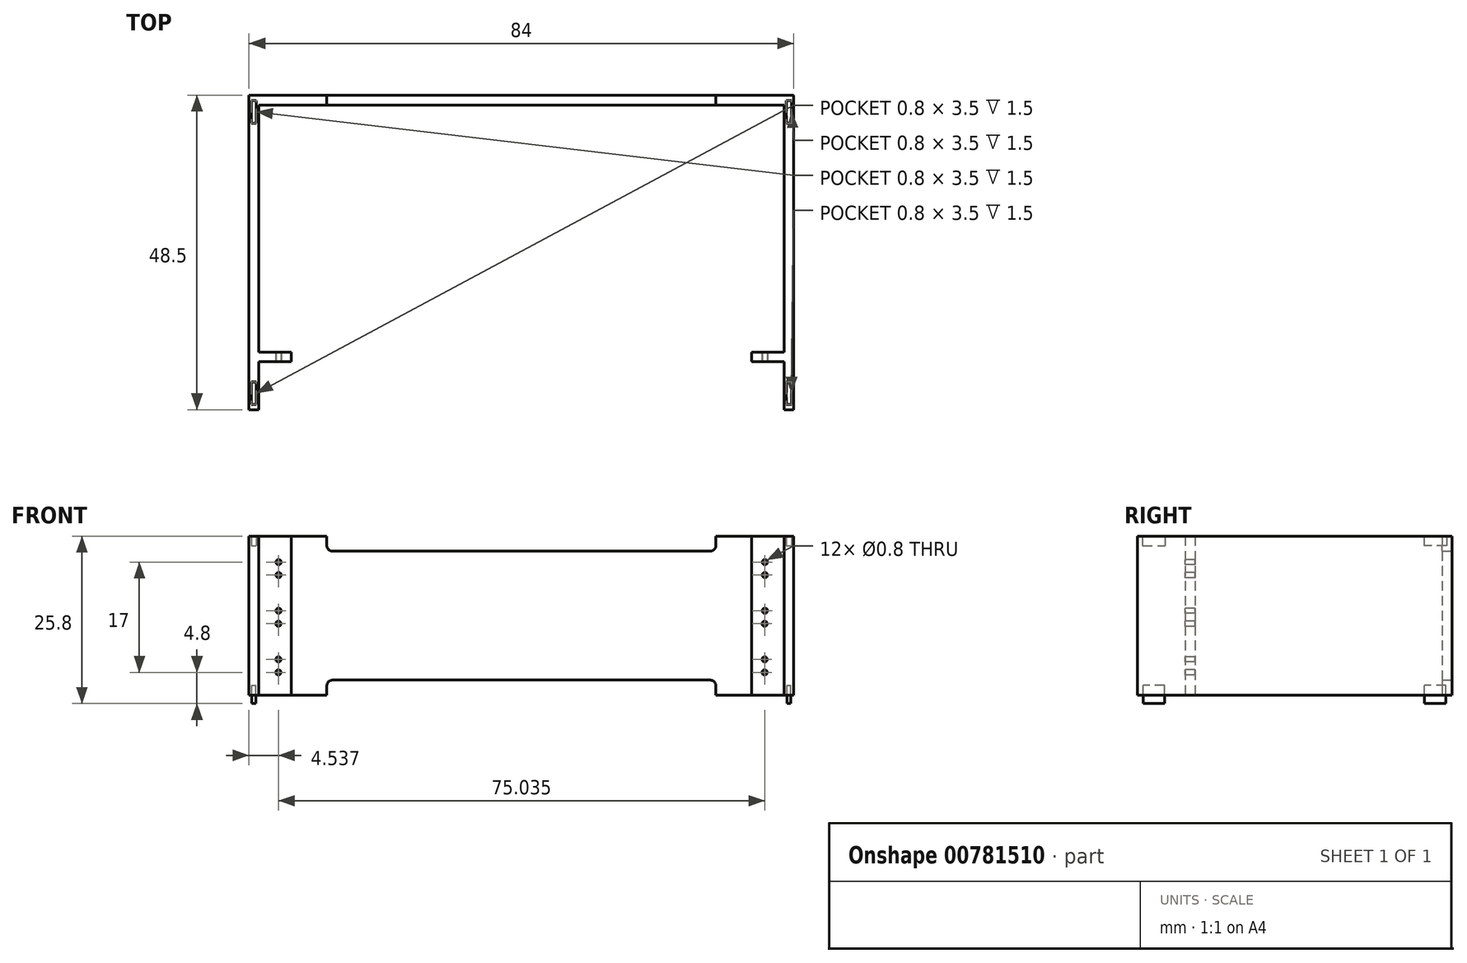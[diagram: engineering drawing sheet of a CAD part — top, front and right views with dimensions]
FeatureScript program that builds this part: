
annotation { "Feature Type Name" : "Feature", "Feature Type Description" : "" }
export const myFeature = defineFeature(function(context is Context, id is Id, definition is map)
    precondition{}
    {
        {
            var Q0;
            Q0=qCreatedBy(makeId("Top.planeOp"),FACE);
            var sketch = newSketch(context, id + "F0", { "sketchPlane" : qUnion([Q0])});
            skLineSegment(sketch, "E0.bottom", {"start": v(-40.55, -23.12) * mm, "end": v(-42.05, -23.12) * mm});
            skLineSegment(sketch, "E0.top", {"start": v(-40.55, 23.88) * mm, "end": v(-42.05, 23.88) * mm});
            skLineSegment(sketch, "E0.left", {"start": v(-40.55, -23.12) * mm, "end": v(-40.55, 23.88) * mm});
            skLineSegment(sketch, "E0.right", {"start": v(-42.05, -23.12) * mm, "end": v(-42.05, 23.88) * mm});
            skLineSegment(sketch, "E1.bottom", {"start": v(40.45, -23.12) * mm, "end": v(41.95, -23.12) * mm});
            skLineSegment(sketch, "E1.top", {"start": v(40.45, 23.88) * mm, "end": v(41.95, 23.88) * mm});
            skLineSegment(sketch, "E1.left", {"start": v(40.45, -23.12) * mm, "end": v(40.45, 23.88) * mm});
            skLineSegment(sketch, "E1.right", {"start": v(41.95, -23.12) * mm, "end": v(41.95, 23.88) * mm});
            skLineSegment(sketch, "E2.bottom", {"start": v(41.95, 23.88) * mm, "end": v(-42.05, 23.88) * mm});
            skLineSegment(sketch, "E2.top", {"start": v(41.95, 25.38) * mm, "end": v(-42.05, 25.38) * mm});
            skLineSegment(sketch, "E2.left", {"start": v(41.95, 23.88) * mm, "end": v(41.95, 25.38) * mm});
            skLineSegment(sketch, "E2.right", {"start": v(-42.05, 23.88) * mm, "end": v(-42.05, 25.38) * mm});
            skLineSegment(sketch, "E3.bottom", {"start": v(-40.55, -14.22) * mm, "end": v(-35.55, -14.22) * mm});
            skLineSegment(sketch, "E3.top", {"start": v(-40.55, -15.72) * mm, "end": v(-35.55, -15.72) * mm});
            skLineSegment(sketch, "E3.left", {"start": v(-40.55, -14.22) * mm, "end": v(-40.55, -15.72) * mm});
            skLineSegment(sketch, "E3.right", {"start": v(-35.55, -14.22) * mm, "end": v(-35.55, -15.72) * mm});
            skLineSegment(sketch, "E4.bottom", {"start": v(35.45, -15.72) * mm, "end": v(40.45, -15.72) * mm});
            skLineSegment(sketch, "E4.top", {"start": v(35.45, -14.22) * mm, "end": v(40.45, -14.22) * mm});
            skLineSegment(sketch, "E4.left", {"start": v(35.45, -15.72) * mm, "end": v(35.45, -14.22) * mm});
            skLineSegment(sketch, "E4.right", {"start": v(40.45, -15.72) * mm, "end": v(40.45, -14.22) * mm});
            skLineSegment(sketch, "E5.bottom", {"start": v(-41.7, -22.32) * mm, "end": v(-40.9, -22.32) * mm});
            skLineSegment(sketch, "E5.top", {"start": v(-41.7, -18.82) * mm, "end": v(-40.9, -18.82) * mm});
            skLineSegment(sketch, "E5.left", {"start": v(-41.7, -22.32) * mm, "end": v(-41.7, -18.82) * mm});
            skLineSegment(sketch, "E5.right", {"start": v(-40.9, -22.32) * mm, "end": v(-40.9, -18.82) * mm});
            skLineSegment(sketch, "E6.bottom", {"start": v(-41.7, 24.58) * mm, "end": v(-40.9, 24.58) * mm});
            skLineSegment(sketch, "E6.top", {"start": v(-41.7, 21.08) * mm, "end": v(-40.9, 21.08) * mm});
            skLineSegment(sketch, "E6.left", {"start": v(-41.7, 24.58) * mm, "end": v(-41.7, 21.08) * mm});
            skLineSegment(sketch, "E6.right", {"start": v(-40.9, 24.58) * mm, "end": v(-40.9, 21.08) * mm});
            skLineSegment(sketch, "E7.bottom", {"start": v(40.8, 24.58) * mm, "end": v(41.6, 24.58) * mm});
            skLineSegment(sketch, "E7.top", {"start": v(40.8, 21.08) * mm, "end": v(41.6, 21.08) * mm});
            skLineSegment(sketch, "E7.left", {"start": v(40.8, 24.58) * mm, "end": v(40.8, 21.08) * mm});
            skLineSegment(sketch, "E7.right", {"start": v(41.6, 24.58) * mm, "end": v(41.6, 21.08) * mm});
            skLineSegment(sketch, "E8.bottom", {"start": v(40.8, -18.82) * mm, "end": v(41.6, -18.82) * mm});
            skLineSegment(sketch, "E8.top", {"start": v(40.8, -22.32) * mm, "end": v(41.6, -22.32) * mm});
            skLineSegment(sketch, "E8.left", {"start": v(40.8, -18.82) * mm, "end": v(40.8, -22.32) * mm});
            skLineSegment(sketch, "E8.right", {"start": v(41.6, -18.82) * mm, "end": v(41.6, -22.32) * mm});
            skLineSegment(sketch, "E9.bottom", {"start": v(-41.6, -18.92) * mm, "end": v(-41, -18.92) * mm});
            skLineSegment(sketch, "E9.top", {"start": v(-41.6, -22.22) * mm, "end": v(-41, -22.22) * mm});
            skLineSegment(sketch, "E9.left", {"start": v(-41.6, -18.92) * mm, "end": v(-41.6, -22.22) * mm});
            skLineSegment(sketch, "E9.right", {"start": v(-41, -18.92) * mm, "end": v(-41, -22.22) * mm});
            skLineSegment(sketch, "E10.bottom", {"start": v(-41.6, 24.48) * mm, "end": v(-41, 24.48) * mm});
            skLineSegment(sketch, "E10.top", {"start": v(-41.6, 21.18) * mm, "end": v(-41, 21.18) * mm});
            skLineSegment(sketch, "E10.left", {"start": v(-41.6, 24.48) * mm, "end": v(-41.6, 21.18) * mm});
            skLineSegment(sketch, "E10.right", {"start": v(-41, 24.48) * mm, "end": v(-41, 21.18) * mm});
            skLineSegment(sketch, "E11.bottom", {"start": v(40.9, 24.48) * mm, "end": v(41.5, 24.48) * mm});
            skLineSegment(sketch, "E11.top", {"start": v(40.9, 21.18) * mm, "end": v(41.5, 21.18) * mm});
            skLineSegment(sketch, "E11.left", {"start": v(40.9, 24.48) * mm, "end": v(40.9, 21.18) * mm});
            skLineSegment(sketch, "E11.right", {"start": v(41.5, 24.48) * mm, "end": v(41.5, 21.18) * mm});
            skLineSegment(sketch, "E12.bottom", {"start": v(40.9, -18.92) * mm, "end": v(41.5, -18.92) * mm});
            skLineSegment(sketch, "E12.top", {"start": v(40.9, -22.22) * mm, "end": v(41.5, -22.22) * mm});
            skLineSegment(sketch, "E12.left", {"start": v(40.9, -18.92) * mm, "end": v(40.9, -22.22) * mm});
            skLineSegment(sketch, "E12.right", {"start": v(41.5, -18.92) * mm, "end": v(41.5, -22.22) * mm});
            skSolve(sketch);
        }
        {
            var Q0;
            Q0=makeQuery(id+"F0.imprint","IMPRINT",FACE,{"disambiguationData":[TD([[makeQuery(id+"F0.imprint","IMPRINT",EDGE,{"derivedFrom":sQuery(id+"F0.wireOp",EDGE,"E3.bottom")}),-1.0]])]});
            var Q1;
            {var subQ5=sQuery(id+"F0.wireOp",EDGE,"E0.bottom");Q1=makeQuery(id+"F0.imprint","IMPRINT",FACE,{"disambiguationData":[TD([[makeQuery(id+"F0.imprint","IMPRINT",EDGE,{"derivedFrom":subQ5}),-1.0]])]});}
            var Q2;
            Q2=makeQuery(id+"F0.imprint","IMPRINT",FACE,{"disambiguationData":[TD([[makeQuery(id+"F0.imprint","IMPRINT",EDGE,{"derivedFrom":sQuery(id+"F0.wireOp",EDGE,"E2.top")}),1.0]])]});
            var Q3;
            {var subQ5=sQuery(id+"F0.wireOp",EDGE,"E1.bottom");Q3=makeQuery(id+"F0.imprint","IMPRINT",FACE,{"disambiguationData":[TD([[makeQuery(id+"F0.imprint","IMPRINT",EDGE,{"derivedFrom":subQ5}),1.0]])]});}
            var Q4;
            Q4=makeQuery(id+"F0.imprint","IMPRINT",FACE,{"disambiguationData":[TD([[makeQuery(id+"F0.imprint","IMPRINT",EDGE,{"derivedFrom":sQuery(id+"F0.wireOp",EDGE,"E4.bottom")}),1.0]])]});
            var Q5;
            Q5=makeQuery(id+"F0.imprint","IMPRINT",FACE,{"disambiguationData":[TD([[makeQuery(id+"F0.imprint","IMPRINT",EDGE,{"derivedFrom":sQuery(id+"F0.wireOp",EDGE,"E5.bottom")}),1.0]])]});
            var Q6;
            Q6=makeQuery(id+"F0.imprint","IMPRINT",FACE,{"disambiguationData":[TD([[makeQuery(id+"F0.imprint","IMPRINT",EDGE,{"derivedFrom":sQuery(id+"F0.wireOp",EDGE,"E8.bottom")}),-1.0]])]});
            var Q7;
            {var subQ5=sQuery(id+"F0.wireOp",EDGE,"E7.top");Q7=makeQuery(id+"F0.imprint","IMPRINT",FACE,{"disambiguationData":[TD([[makeQuery(id+"F0.imprint","IMPRINT",EDGE,{"derivedFrom":subQ5}),1.0]])]});}
            var Q8;
            {var subQ5=sQuery(id+"F0.wireOp",EDGE,"E7.bottom");Q8=makeQuery(id+"F0.imprint","IMPRINT",FACE,{"disambiguationData":[TD([[makeQuery(id+"F0.imprint","IMPRINT",EDGE,{"derivedFrom":subQ5}),-1.0]])]});}
            var Q9;
            {var subQ5=sQuery(id+"F0.wireOp",EDGE,"E6.bottom");Q9=makeQuery(id+"F0.imprint","IMPRINT",FACE,{"disambiguationData":[TD([[makeQuery(id+"F0.imprint","IMPRINT",EDGE,{"derivedFrom":subQ5}),-1.0]])]});}
            var Q10;
            {var subQ5=sQuery(id+"F0.wireOp",EDGE,"E6.top");Q10=makeQuery(id+"F0.imprint","IMPRINT",FACE,{"disambiguationData":[TD([[makeQuery(id+"F0.imprint","IMPRINT",EDGE,{"derivedFrom":subQ5}),1.0]])]});}
            var Q11;
            Q11=makeQuery(id+"F0.imprint","IMPRINT",FACE,{"disambiguationData":[TD([[makeQuery(id+"F0.imprint","IMPRINT",EDGE,{"derivedFrom":sQuery(id+"F0.wireOp",EDGE,"E9.bottom")}),-1.0]])]});
            var Q12;
            {var subQ5=sQuery(id+"F0.wireOp",EDGE,"E10.top");Q12=makeQuery(id+"F0.imprint","IMPRINT",FACE,{"disambiguationData":[TD([[makeQuery(id+"F0.imprint","IMPRINT",EDGE,{"derivedFrom":subQ5}),1.0]])]});}
            var Q13;
            Q13=makeQuery(id+"F0.imprint","IMPRINT",FACE,{"disambiguationData":[TD([[makeQuery(id+"F0.imprint","IMPRINT",EDGE,{"derivedFrom":sQuery(id+"F0.wireOp",EDGE,"E12.bottom")}),-1.0]])]});
            var Q14;
            {var subQ5=sQuery(id+"F0.wireOp",EDGE,"E11.top");Q14=makeQuery(id+"F0.imprint","IMPRINT",FACE,{"disambiguationData":[TD([[makeQuery(id+"F0.imprint","IMPRINT",EDGE,{"derivedFrom":subQ5}),1.0]])]});}
            var Q15;
            {var subQ5=sQuery(id+"F0.wireOp",EDGE,"E11.bottom");Q15=makeQuery(id+"F0.imprint","IMPRINT",FACE,{"disambiguationData":[TD([[makeQuery(id+"F0.imprint","IMPRINT",EDGE,{"derivedFrom":subQ5}),-1.0]])]});}
            var Q16;
            {var subQ5=sQuery(id+"F0.wireOp",EDGE,"E10.bottom");Q16=makeQuery(id+"F0.imprint","IMPRINT",FACE,{"disambiguationData":[TD([[makeQuery(id+"F0.imprint","IMPRINT",EDGE,{"derivedFrom":subQ5}),-1.0]])]});}
            extrude(context, id + "F1", {"entities" : qUnion([Q0, Q1, Q2, Q3, Q4, Q5, Q6, Q7, Q8, Q9, Q10, Q11, Q12, Q13, Q14, Q15, Q16]), "depth" : 23 * mm, "offsetDistance" : 25 * mm, "hasSecondDirection" : true, "secondDirectionOppositeDirection" : true, "secondDirectionDepth" : 1.5 * mm});
        }
        {
            var Q0;
            Q0=makeQuery(id+"F1.opExtrude","SWEPT_FACE",FACE,{"disambiguationData":[OSD([sQuery(id+"F0.wireOp",EDGE,"E3.top")])]});
            var sketch = newSketch(context, id + "F2", { "sketchPlane" : qUnion([Q0])});
            skPoint(sketch, "E13", {"position": v(-37.51, 4) * mm});
            skPoint(sketch, "E14", {"position": v(-37.51, 2) * mm});
            skPoint(sketch, "E15", {"position": v(-37.48, 11.5) * mm});
            skPoint(sketch, "E16", {"position": v(-37.51, 9.5) * mm});
            skPoint(sketch, "E17", {"position": v(-37.48, 19) * mm});
            skPoint(sketch, "E18", {"position": v(-37.48, 17) * mm});
            skSolve(sketch);
        }
        {
            var Q0;
            Q0=sQuery(id+"F2.wireOp",VERTEX,"88589781-5102-4832-97d8-1e510481dceb");
            var Q1;
            Q1=sQuery(id+"F2.wireOp",VERTEX,"56790afe-c75e-4d87-a7f2-a835bb2694d8");
            var Q2;
            Q2=sQuery(id+"F2.wireOp",VERTEX,"4a0b0304-49c9-424d-a3fc-b7b72423f08e");
            var Q3;
            Q3=sQuery(id+"F2.wireOp",VERTEX,"8470db93-98b9-4a33-af80-0723f33e9908");
            var Q4;
            Q4=sQuery(id+"F2.wireOp",VERTEX,"2e0e3efe-daf6-4547-b27c-54efc526473a");
            var Q5;
            Q5=sQuery(id+"F2.wireOp",VERTEX,"7f74d1a5-d060-45e6-a30a-b5d7ec352d9f");
            var Q6;
            Q6=sQuery(id+"F2.wireOp",VERTEX,"e7f13f87-68be-49df-9cb8-7ec9ecd05ca7");
            var Q7;
            Q7=sQuery(id+"F2.wireOp",VERTEX,"4bbd2e0c-c852-44a6-b9f7-45fbe5631dce");
            var Q8;
            Q8=sQuery(id+"F2.wireOp",VERTEX,"ba70f5e1-98a7-43c2-a71f-77c1e018e1af");
            var Q9;
            Q9=sQuery(id+"F2.wireOp",VERTEX,"cb561a4e-391f-4cf2-8014-02b8de1940b7");
            var Q10;
            Q10=sQuery(id+"F2.wireOp",VERTEX,"25fe7e44-f2c1-4e66-bf82-ea21deba93e5");
            var Q11;
            Q11=sQuery(id+"F2.wireOp",VERTEX,"d46ec7f3-1b37-4474-b349-0d3c5d30f0cb");
            var Q12;
            Q12=sQuery(id+"F2.wireOp",VERTEX,"1438e96a-6f7b-4250-b74d-4fb95acfcb2b");
            var Q13;
            Q13=sQuery(id+"F2.wireOp",VERTEX,"121fa19b-167c-4f1e-bf5a-e0e98d88baee");
            var Q14;
            Q14=sQuery(id+"F2.wireOp",VERTEX,"675ebcd7-a57f-4c2a-8b93-9ba6a5267821");
            var Q15;
            Q15=sQuery(id+"F2.wireOp",VERTEX,"1d6a26b5-c100-4562-8f77-8e2f2a2a09b2");
            var Q16;
            Q16=sQuery(id+"F2.wireOp",VERTEX,"6a4d0978-3533-43de-9fda-7213b88e7c2f");
            var Q17;
            Q17=sQuery(id+"F2.wireOp",VERTEX,"3fb22aad-e230-4993-b6bc-54e331a05df5");
            var Q18;
            Q18=sQuery(id+"F2.wireOp",VERTEX,"15e36bbe-4873-47a5-a130-d166c739b6b5");
            var Q19;
            Q19=sQuery(id+"F2.wireOp",VERTEX,"246902ba-4f59-4fde-931c-b349720525bf");
            var Q20;
            Q20=sQuery(id+"F2.wireOp",VERTEX,"a499105e-2996-41cf-a285-387e233015b6");
            var Q21;
            Q21=sQuery(id+"F2.wireOp",VERTEX,"672db32d-2f95-4abb-8e6e-725b967cd659");
            var Q22;
            Q22=sQuery(id+"F2.wireOp",VERTEX,"16b57b02-6109-4387-9544-32c3ac3d10b3");
            var Q23;
            Q23=sQuery(id+"F2.wireOp",VERTEX,"dd325801-9fbc-4868-b01f-ac81e2aff74c");
            var Q24;
            Q24=sQuery(id+"F2.wireOp",VERTEX,"cb646fc5-ffde-4365-8959-c24c6d32095a");
            var Q25;
            Q25=sQuery(id+"F2.wireOp",VERTEX,"feb0eac7-72ea-407a-bd9d-7e842050beeb");
            var Q26;
            Q26=sQuery(id+"F2.wireOp",VERTEX,"E17");
            var Q27;
            Q27=sQuery(id+"F2.wireOp",VERTEX,"E18");
            var Q28;
            Q28=sQuery(id+"F2.wireOp",VERTEX,"E15");
            var Q29;
            Q29=sQuery(id+"F2.wireOp",VERTEX,"E16");
            var Q30;
            Q30=sQuery(id+"F2.wireOp",VERTEX,"E13");
            var Q31;
            Q31=sQuery(id+"F2.wireOp",VERTEX,"E14");
            var Q32;
            Q32=makeQuery(id+"F1.opExtrude","SWEPT_BODY",BODY,{"disambiguationData":[OSD([sQuery(id+"F0.wireOp",EDGE,"E0.bottom"),sQuery(id+"F0.wireOp",EDGE,"E0.left"),sQuery(id+"F0.wireOp",EDGE,"E0.right"),sQuery(id+"F0.wireOp",EDGE,"E1.bottom"),sQuery(id+"F0.wireOp",EDGE,"E1.left"),sQuery(id+"F0.wireOp",EDGE,"E1.right"),sQuery(id+"F0.wireOp",EDGE,"E2.bottom"),sQuery(id+"F0.wireOp",EDGE,"E2.top"),sQuery(id+"F0.wireOp",EDGE,"E2.left"),sQuery(id+"F0.wireOp",EDGE,"E2.right"),sQuery(id+"F0.wireOp",EDGE,"E3.bottom"),sQuery(id+"F0.wireOp",EDGE,"E3.top"),sQuery(id+"F0.wireOp",EDGE,"E3.right"),sQuery(id+"F0.wireOp",EDGE,"E4.bottom"),sQuery(id+"F0.wireOp",EDGE,"E4.top"),sQuery(id+"F0.wireOp",EDGE,"E4.left")])]});
            hole(context, id + "F3", {"style" : HoleStyle.SIMPLE, "endStyle" : HoleEndStyle.BLIND, "holeDiameter" : .8 * mm, "majorDiameter" : 5 * mm, "holeDepth" : 2 * mm, "isTappedThrough" : true, "tappedDepth" : 12 * mm, "tapClearance" : 3, "locations" : qUnion([Q0, Q1, Q2, Q3, Q4, Q5, Q6, Q7, Q8, Q9, Q10, Q11, Q12, Q13, Q14, Q15, Q16, Q17, Q18, Q19, Q20, Q21, Q22, Q23, Q24, Q25, Q26, Q27, Q28, Q29, Q30, Q31]), "scope" : qUnion([Q32])});
        }
        {
            var Q0;
            Q0=makeQuery(id+"F1.opExtrude","SWEPT_FACE",FACE,{"disambiguationData":[OSD([sQuery(id+"F0.wireOp",EDGE,"E4.bottom")])]});
            var sketch = newSketch(context, id + "F4", { "sketchPlane" : qUnion([Q0])});
            skPoint(sketch, "E19", {"position": v(37.47, 4) * mm});
            skPoint(sketch, "E20", {"position": v(37.47, 2) * mm});
            skPoint(sketch, "E21", {"position": v(37.52, 11.5) * mm});
            skPoint(sketch, "E22", {"position": v(37.47, 9.5) * mm});
            skPoint(sketch, "E23", {"position": v(37.52, 19) * mm});
            skPoint(sketch, "E24", {"position": v(37.52, 17) * mm});
            skSolve(sketch);
        }
        {
            var Q0;
            Q0=sQuery(id+"F4.wireOp",VERTEX,"1685a108-1c22-47cb-86ea-99102d504769");
            var Q1;
            Q1=sQuery(id+"F4.wireOp",VERTEX,"282c8ce4-5a98-4039-a490-7a464b3db2a2");
            var Q2;
            Q2=sQuery(id+"F4.wireOp",VERTEX,"7c48063c-eca5-4a72-9866-b2de93acb628");
            var Q3;
            Q3=sQuery(id+"F4.wireOp",VERTEX,"93b985b0-b66a-4ae3-be20-7b9a7e3f2b6c");
            var Q4;
            Q4=sQuery(id+"F4.wireOp",VERTEX,"cc428c83-d56d-4959-b9be-0128fded5aa7");
            var Q5;
            Q5=sQuery(id+"F4.wireOp",VERTEX,"923acce6-366c-4c4e-bd52-c46ad51c2bb4");
            var Q6;
            Q6=sQuery(id+"F4.wireOp",VERTEX,"342c2384-4a72-4381-ae02-47dd513850cd");
            var Q7;
            Q7=sQuery(id+"F4.wireOp",VERTEX,"a94b797b-b7a0-4b5d-b07a-f5b021580715");
            var Q8;
            Q8=sQuery(id+"F4.wireOp",VERTEX,"d03c6149-6b66-4745-8704-c4af4b69b51a");
            var Q9;
            Q9=sQuery(id+"F4.wireOp",VERTEX,"ab94b1e0-753a-426b-84fc-aa24667ea698");
            var Q10;
            Q10=sQuery(id+"F4.wireOp",VERTEX,"1abd8f64-ad39-4732-ba89-73d322f6d9b7");
            var Q11;
            Q11=sQuery(id+"F4.wireOp",VERTEX,"f42cbf2c-5cc6-48a4-9d8f-f00945ee456c");
            var Q12;
            Q12=sQuery(id+"F4.wireOp",VERTEX,"406a435b-751b-42b4-8a9d-1317aad79ab7");
            var Q13;
            Q13=sQuery(id+"F4.wireOp",VERTEX,"6d304315-1eab-46f7-9fc0-8e03bbc8edbb");
            var Q14;
            Q14=sQuery(id+"F4.wireOp",VERTEX,"b954348f-f6c4-4487-94ef-fc340416bc01");
            var Q15;
            Q15=sQuery(id+"F4.wireOp",VERTEX,"562790b9-a17d-4935-b5ba-e2a4e6fc7c41");
            var Q16;
            Q16=sQuery(id+"F4.wireOp",VERTEX,"11ccae4c-fa3e-447b-9bf8-9337cd2bc9b2");
            var Q17;
            Q17=sQuery(id+"F4.wireOp",VERTEX,"34ad80a4-5b65-4afb-bad3-842bd72bae2e");
            var Q18;
            Q18=sQuery(id+"F4.wireOp",VERTEX,"3f396bc3-fa41-4e3c-a7ad-04af7e7c270f");
            var Q19;
            Q19=sQuery(id+"F4.wireOp",VERTEX,"25eeea29-f4b8-45e0-a54d-9ec8ff17cd8f");
            var Q20;
            Q20=sQuery(id+"F4.wireOp",VERTEX,"af4ec9f9-d0a4-46eb-8cca-ffa83608b68e");
            var Q21;
            Q21=sQuery(id+"F4.wireOp",VERTEX,"40076fb2-e2af-41ad-a221-b252a0a85449");
            var Q22;
            Q22=sQuery(id+"F4.wireOp",VERTEX,"8c5c71d5-6768-4dcb-961d-44b3619711e2");
            var Q23;
            Q23=sQuery(id+"F4.wireOp",VERTEX,"e79863dc-fafb-41b5-8f80-bdf207221749");
            var Q24;
            Q24=sQuery(id+"F4.wireOp",VERTEX,"59ef7793-e199-40ab-b9b7-da37e43eeb6f");
            var Q25;
            Q25=sQuery(id+"F4.wireOp",VERTEX,"5bd304c4-b3ee-47e3-a3fb-79a97eea6e25");
            var Q26;
            Q26=sQuery(id+"F4.wireOp",VERTEX,"E23");
            var Q27;
            Q27=sQuery(id+"F4.wireOp",VERTEX,"E24");
            var Q28;
            Q28=sQuery(id+"F4.wireOp",VERTEX,"E21");
            var Q29;
            Q29=sQuery(id+"F4.wireOp",VERTEX,"E22");
            var Q30;
            Q30=sQuery(id+"F4.wireOp",VERTEX,"E19");
            var Q31;
            Q31=sQuery(id+"F4.wireOp",VERTEX,"E20");
            var Q32;
            Q32=makeQuery(id+"F1.opExtrude","SWEPT_BODY",BODY,{"disambiguationData":[OSD([sQuery(id+"F0.wireOp",EDGE,"E0.bottom"),sQuery(id+"F0.wireOp",EDGE,"E0.left"),sQuery(id+"F0.wireOp",EDGE,"E0.right"),sQuery(id+"F0.wireOp",EDGE,"E1.bottom"),sQuery(id+"F0.wireOp",EDGE,"E1.left"),sQuery(id+"F0.wireOp",EDGE,"E1.right"),sQuery(id+"F0.wireOp",EDGE,"E2.bottom"),sQuery(id+"F0.wireOp",EDGE,"E2.top"),sQuery(id+"F0.wireOp",EDGE,"E2.left"),sQuery(id+"F0.wireOp",EDGE,"E2.right"),sQuery(id+"F0.wireOp",EDGE,"E3.bottom"),sQuery(id+"F0.wireOp",EDGE,"E3.top"),sQuery(id+"F0.wireOp",EDGE,"E3.right"),sQuery(id+"F0.wireOp",EDGE,"E4.bottom"),sQuery(id+"F0.wireOp",EDGE,"E4.top"),sQuery(id+"F0.wireOp",EDGE,"E4.left")])]});
            hole(context, id + "F5", {"style" : HoleStyle.SIMPLE, "endStyle" : HoleEndStyle.BLIND, "holeDiameter" : .8 * mm, "majorDiameter" : 5 * mm, "holeDepth" : 2 * mm, "isTappedThrough" : true, "tappedDepth" : 12 * mm, "tapClearance" : 3, "locations" : qUnion([Q0, Q1, Q2, Q3, Q4, Q5, Q6, Q7, Q8, Q9, Q10, Q11, Q12, Q13, Q14, Q15, Q16, Q17, Q18, Q19, Q20, Q21, Q22, Q23, Q24, Q25, Q26, Q27, Q28, Q29, Q30, Q31]), "scope" : qUnion([Q32])});
        }
        {
            var Q0;
            {var subQ5=sQuery(id+"F0.wireOp",EDGE,"E10.top");Q0=makeQuery(id+"F0.imprint","IMPRINT",FACE,{"disambiguationData":[TD([[makeQuery(id+"F0.imprint","IMPRINT",EDGE,{"derivedFrom":subQ5}),1.0]])]});}
            var Q1;
            {var subQ5=sQuery(id+"F0.wireOp",EDGE,"E10.bottom");Q1=makeQuery(id+"F0.imprint","IMPRINT",FACE,{"disambiguationData":[TD([[makeQuery(id+"F0.imprint","IMPRINT",EDGE,{"derivedFrom":subQ5}),-1.0]])]});}
            var Q2;
            Q2=makeQuery(id+"F0.imprint","IMPRINT",FACE,{"disambiguationData":[TD([[makeQuery(id+"F0.imprint","IMPRINT",EDGE,{"derivedFrom":sQuery(id+"F0.wireOp",EDGE,"E9.bottom")}),-1.0]])]});
            var Q3;
            {var subQ5=sQuery(id+"F0.wireOp",EDGE,"E11.top");Q3=makeQuery(id+"F0.imprint","IMPRINT",FACE,{"disambiguationData":[TD([[makeQuery(id+"F0.imprint","IMPRINT",EDGE,{"derivedFrom":subQ5}),1.0]])]});}
            var Q4;
            {var subQ5=sQuery(id+"F0.wireOp",EDGE,"E11.bottom");Q4=makeQuery(id+"F0.imprint","IMPRINT",FACE,{"disambiguationData":[TD([[makeQuery(id+"F0.imprint","IMPRINT",EDGE,{"derivedFrom":subQ5}),-1.0]])]});}
            var Q5;
            Q5=makeQuery(id+"F0.imprint","IMPRINT",FACE,{"disambiguationData":[TD([[makeQuery(id+"F0.imprint","IMPRINT",EDGE,{"derivedFrom":sQuery(id+"F0.wireOp",EDGE,"E12.bottom")}),-1.0]])]});
            extrude(context, id + "F6", {"entities" : qUnion([Q0, Q1, Q2, Q3, Q4, Q5]), "oppositeDirection" : true, "depth" : 2.8 * mm, "offsetDistance" : 25 * mm});
        }
        {
            var Q0;
            Q0=makeQuery(id+"F0.imprint","IMPRINT",FACE,{"disambiguationData":[TD([[makeQuery(id+"F0.imprint","IMPRINT",EDGE,{"derivedFrom":sQuery(id+"F0.wireOp",EDGE,"E5.bottom")}),1.0]])]});
            var Q1;
            {var subQ5=sQuery(id+"F0.wireOp",EDGE,"E7.bottom");Q1=makeQuery(id+"F0.imprint","IMPRINT",FACE,{"disambiguationData":[TD([[makeQuery(id+"F0.imprint","IMPRINT",EDGE,{"derivedFrom":subQ5}),-1.0]])]});}
            var Q2;
            {var subQ5=sQuery(id+"F0.wireOp",EDGE,"E10.top");Q2=makeQuery(id+"F0.imprint","IMPRINT",FACE,{"disambiguationData":[TD([[makeQuery(id+"F0.imprint","IMPRINT",EDGE,{"derivedFrom":subQ5}),1.0]])]});}
            var Q3;
            {var subQ1=sQuery(id+"F0.wireOp",EDGE,"E6.top");Q3=makeQuery(id+"F0.imprint","IMPRINT",FACE,{"disambiguationData":[TD([[makeQuery(id+"F0.imprint","IMPRINT",EDGE,{"derivedFrom":subQ1}),1.0]])]});}
            var Q4;
            {var subQ5=sQuery(id+"F0.wireOp",EDGE,"E10.bottom");Q4=makeQuery(id+"F0.imprint","IMPRINT",FACE,{"disambiguationData":[TD([[makeQuery(id+"F0.imprint","IMPRINT",EDGE,{"derivedFrom":subQ5}),-1.0]])]});}
            var Q5;
            {var subQ1=sQuery(id+"F0.wireOp",EDGE,"E6.bottom");Q5=makeQuery(id+"F0.imprint","IMPRINT",FACE,{"disambiguationData":[TD([[makeQuery(id+"F0.imprint","IMPRINT",EDGE,{"derivedFrom":subQ1}),-1.0]])]});}
            var Q6;
            Q6=makeQuery(id+"F0.imprint","IMPRINT",FACE,{"disambiguationData":[TD([[makeQuery(id+"F0.imprint","IMPRINT",EDGE,{"derivedFrom":sQuery(id+"F0.wireOp",EDGE,"E9.bottom")}),-1.0]])]});
            var Q7;
            Q7=makeQuery(id+"F0.imprint","IMPRINT",FACE,{"disambiguationData":[TD([[makeQuery(id+"F0.imprint","IMPRINT",EDGE,{"derivedFrom":sQuery(id+"F0.wireOp",EDGE,"E12.bottom")}),-1.0]])]});
            var Q8;
            Q8=makeQuery(id+"F0.imprint","IMPRINT",FACE,{"disambiguationData":[TD([[makeQuery(id+"F0.imprint","IMPRINT",EDGE,{"derivedFrom":sQuery(id+"F0.wireOp",EDGE,"E8.bottom")}),-1.0]])]});
            var Q9;
            {var subQ1=sQuery(id+"F0.wireOp",EDGE,"E7.top");Q9=makeQuery(id+"F0.imprint","IMPRINT",FACE,{"disambiguationData":[TD([[makeQuery(id+"F0.imprint","IMPRINT",EDGE,{"derivedFrom":subQ1}),1.0]])]});}
            var Q10;
            {var subQ5=sQuery(id+"F0.wireOp",EDGE,"E11.top");Q10=makeQuery(id+"F0.imprint","IMPRINT",FACE,{"disambiguationData":[TD([[makeQuery(id+"F0.imprint","IMPRINT",EDGE,{"derivedFrom":subQ5}),1.0]])]});}
            var Q11;
            {var subQ5=sQuery(id+"F0.wireOp",EDGE,"E11.bottom");Q11=makeQuery(id+"F0.imprint","IMPRINT",FACE,{"disambiguationData":[TD([[makeQuery(id+"F0.imprint","IMPRINT",EDGE,{"derivedFrom":subQ5}),-1.0]])]});}
            extrude(context, id + "F7", {"entities" : qUnion([Q0, Q1, Q2, Q3, Q4, Q5, Q6, Q7, Q8, Q9, Q10, Q11]), "operationType" : NewBodyOperationType.REMOVE, "depth" : 23 * mm, "offsetDistance" : 25 * mm, "hasSecondDirection" : true, "secondDirectionOppositeDirection" : false, "secondDirectionDepth" : 21.5 * mm});
        }
        {
            var Q0;
            Q0=makeQuery(id+"F1.opExtrude","SWEPT_FACE",FACE,{"disambiguationData":[OSD([sQuery(id+"F0.wireOp",EDGE,"E2.top")])]});
            var sketch = newSketch(context, id + "F8", { "sketchPlane" : qUnion([Q0])});
            skLineSegment(sketch, "E25.bottom", {"start": v(-29.05, 20.69) * mm, "end": v(29.15, 20.69) * mm});
            skLineSegment(sketch, "E25.top", {"start": v(-29.95, 23) * mm, "end": v(30.05, 23) * mm});
            skLineSegment(sketch, "E25.left", {"start": v(-29.95, 21.59) * mm, "end": v(-29.95, 23) * mm});
            skLineSegment(sketch, "E25.right", {"start": v(30.05, 21.59) * mm, "end": v(30.05, 23) * mm});
            skLineSegment(sketch, "E26.bottom", {"start": v(-29.95, -1.5) * mm, "end": v(30.05, -1.5) * mm});
            skLineSegment(sketch, "E26.top", {"start": v(-29.05, 0.81) * mm, "end": v(29.15, 0.81) * mm});
            skLineSegment(sketch, "E26.left", {"start": v(-29.95, -1.5) * mm, "end": v(-29.95, -0.09) * mm});
            skLineSegment(sketch, "E26.right", {"start": v(30.05, -1.5) * mm, "end": v(30.05, -0.09) * mm});
            skPoint(sketch, "E27.visualSharp", {"position": v(-29.95, 20.69) * mm});
            skArc(sketch, "E27.filletArc", {"start": v(-29.95, 21.59) * mm, "mid": v(-29.7, 20.95) * mm, "end": v(-29.05, 20.69) * mm});
            skPoint(sketch, "E28.visualSharp", {"position": v(30.05, 20.69) * mm});
            skArc(sketch, "E28.filletArc", {"start": v(29.15, 20.69) * mm, "mid": v(29.78, 20.95) * mm, "end": v(30.05, 21.59) * mm});
            skPoint(sketch, "E29.visualSharp", {"position": v(30.05, 0.81) * mm});
            skArc(sketch, "E29.filletArc", {"start": v(30.05, -0.09) * mm, "mid": v(29.78, 0.55) * mm, "end": v(29.15, 0.81) * mm});
            skPoint(sketch, "E30.visualSharp", {"position": v(-29.95, 0.81) * mm});
            skArc(sketch, "E30.filletArc", {"start": v(-29.05, 0.81) * mm, "mid": v(-29.7, 0.55) * mm, "end": v(-29.95, -0.09) * mm});
            skSolve(sketch);
        }
        {
            var Q0;
            Q0 = qSketchRegion(id + "F8", true);
            extrude(context, id + "F9", {"entities" : qUnion([Q0]), "operationType" : NewBodyOperationType.REMOVE, "oppositeDirection" : true, "depth" : 2 * mm, "offsetDistance" : 25 * mm});
        }
    });
